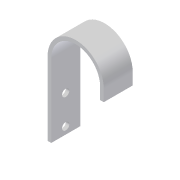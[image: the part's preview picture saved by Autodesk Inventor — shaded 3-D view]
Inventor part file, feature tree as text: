
AUTODESK INVENTOR PART (.ipt)
format: ipt  version: 2012 (Build 160160000, 160)  size: 84,480 bytes
history: native  units: in
note: dims shown in document units (in); Inventor stores cm internally (conversion verified against a paired STEP export)
features: extrude x1, hole x1, pattern_linear x1, sketch x1
ambient origin geometry x8: Origin, YZ Plane, XZ Plane, XY Plane, X Axis, Y Axis, Z Axis, Center Point
bodies: Solid1 (feature_tree)
feature tree (4):
  extrude  "Extrusion1"  Depth=3.5in
  hole  "Hole1"  [1 undecoded]
  pattern_linear  "Rectangular Pattern1"  Spacing1=1.375in  [1 undecoded]
  sketch  "Sketch1"  dims[d0=0.125in d1=3.5in d2=0.8438in d3=1.375in d4=1.0in d5=0.0in d6=0.5in d7=0.25in d8=0.25in d9=0.5in d10=0.375in d11=0.25in d12=0.5635in d13=0.75in d14=0.8108in d15=0.7874in d17=1.0in]
note: 2 required parameter values undecoded (feature->parameter linkage not recoverable at this tier; creation-order binding heuristic only, values carry confidence <= 0.55)
